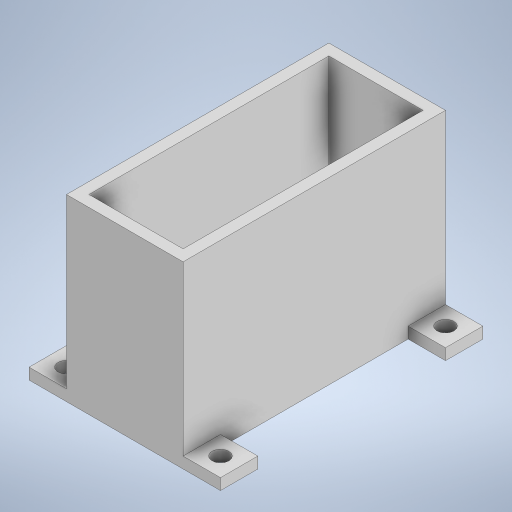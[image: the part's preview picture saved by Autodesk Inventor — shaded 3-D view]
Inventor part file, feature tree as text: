
AUTODESK INVENTOR PART (.ipt)
format: ipt  version: 2024 (Build 280153000, 153)  size: 236,544 bytes
history: native  units: mm
features: extrude x2, sketch x2
ambient origin geometry x8: Origin, YZ Plane, XZ Plane, XY Plane, X Axis, Y Axis, Z Axis, Center Point
bodies: Solid1 (feature_tree)
feature tree (4):
  extrude  "Extrusion1"  Depth=64.2mm
  extrude  "Extrusion2"  Depth=45.0mm TaperAngle=0.0deg
  sketch  "Sketch1"  dims[d0=25.2mm d1=64.2mm]
  sketch  "Sketch2"  dims[d2=3.0mm d3=45.0mm d4=0.0mm d5=4.5mm d6=10.0mm d7=10.0mm d8=5.0mm d9=5.0mm d10=3.0mm d11=0.0mm]
